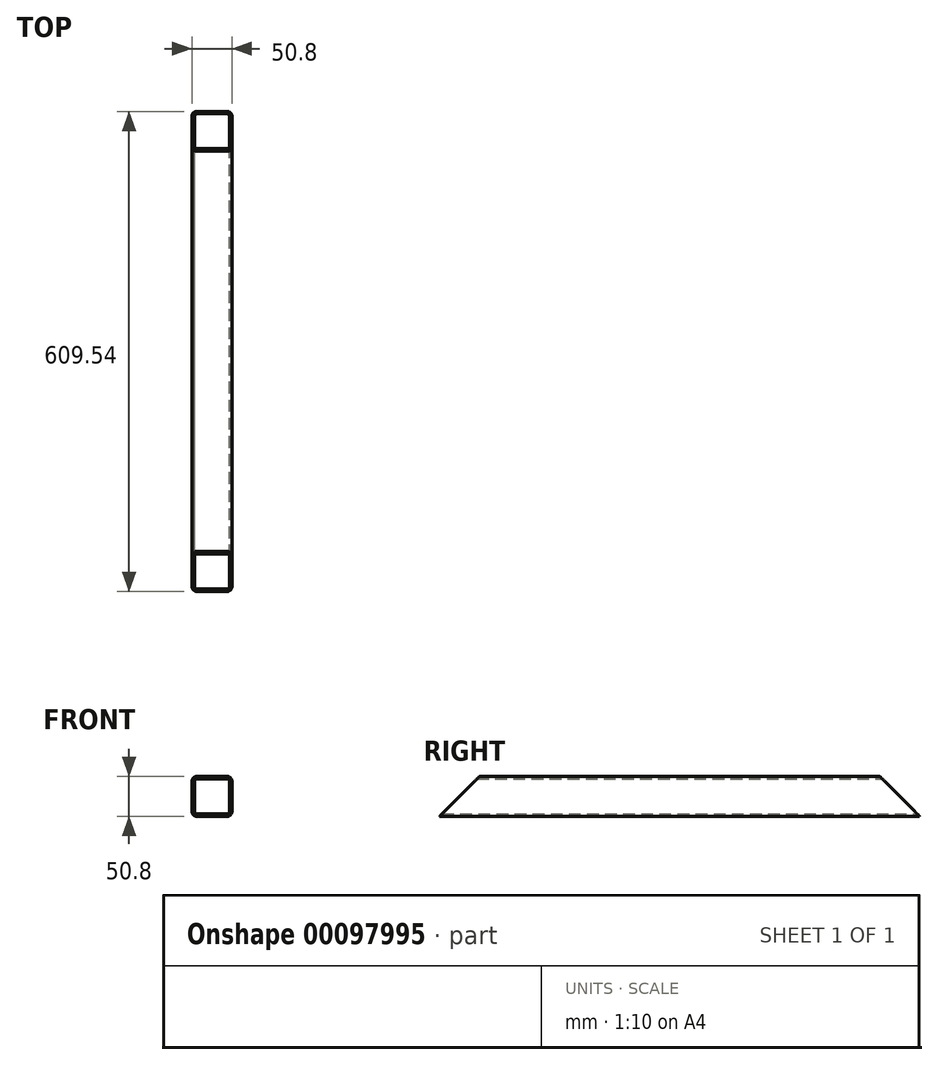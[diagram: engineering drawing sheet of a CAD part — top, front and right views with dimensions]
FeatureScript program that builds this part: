
annotation { "Feature Type Name" : "Feature", "Feature Type Description" : "" }
export const myFeature = defineFeature(function(context is Context, id is Id, definition is map)
    precondition{}
    {
        {
            var Q0;
            Q0=qCreatedBy(makeId("Front.planeOp"),FACE);
            var sketch = newSketch(context, id + "F0", { "sketchPlane" : qUnion([Q0])});
            skLineSegment(sketch, "E0.bottom", {"start": v(19.14, -25.27) * mm, "end": v(-18.96, -25.27) * mm});
            skLineSegment(sketch, "E0.top", {"start": v(19.14, 25.53) * mm, "end": v(-18.96, 25.53) * mm});
            skLineSegment(sketch, "E0.left", {"start": v(25.49, -18.92) * mm, "end": v(25.49, 19.18) * mm});
            skLineSegment(sketch, "E0.right", {"start": v(-25.31, -18.92) * mm, "end": v(-25.31, 19.18) * mm});
            skPoint(sketch, "E0.middle", {"position": v(0.09, 0.13) * mm});
            skLineSegment(sketch, "E1.bottom", {"start": v(19.14, 22.35) * mm, "end": v(-18.96, 22.35) * mm});
            skLineSegment(sketch, "E1.top", {"start": v(19.14, -22.1) * mm, "end": v(-18.96, -22.1) * mm});
            skLineSegment(sketch, "E1.left", {"start": v(22.31, 19.18) * mm, "end": v(22.31, -18.92) * mm});
            skLineSegment(sketch, "E1.right", {"start": v(-22.14, 19.18) * mm, "end": v(-22.14, -18.92) * mm});
            skPoint(sketch, "E2.visualSharp", {"position": v(-25.31, 25.53) * mm});
            skArc(sketch, "E2.filletArc", {"start": v(-18.96, 25.53) * mm, "mid": v(-23.45, 23.67) * mm, "end": v(-25.31, 19.18) * mm});
            skPoint(sketch, "E3.visualSharp", {"position": v(25.49, 25.53) * mm});
            skArc(sketch, "E3.filletArc", {"start": v(25.49, 19.18) * mm, "mid": v(23.63, 23.67) * mm, "end": v(19.14, 25.53) * mm});
            skPoint(sketch, "E4.visualSharp", {"position": v(25.49, -25.27) * mm});
            skArc(sketch, "E4.filletArc", {"start": v(19.14, -25.27) * mm, "mid": v(23.63, -23.41) * mm, "end": v(25.49, -18.92) * mm});
            skPoint(sketch, "E5.visualSharp", {"position": v(-25.31, -25.27) * mm});
            skArc(sketch, "E5.filletArc", {"start": v(-25.31, -18.92) * mm, "mid": v(-23.45, -23.41) * mm, "end": v(-18.96, -25.27) * mm});
            skPoint(sketch, "E6.visualSharp", {"position": v(22.31, 22.35) * mm});
            skArc(sketch, "E6.filletArc", {"start": v(22.31, 19.18) * mm, "mid": v(21.38, 21.42) * mm, "end": v(19.14, 22.35) * mm});
            skPoint(sketch, "E7.visualSharp", {"position": v(22.31, -22.1) * mm});
            skArc(sketch, "E7.filletArc", {"start": v(19.14, -22.1) * mm, "mid": v(21.38, -21.17) * mm, "end": v(22.31, -18.92) * mm});
            skPoint(sketch, "E8.visualSharp", {"position": v(-22.14, -22.1) * mm});
            skArc(sketch, "E8.filletArc", {"start": v(-22.14, -18.92) * mm, "mid": v(-21.2, -21.17) * mm, "end": v(-18.96, -22.1) * mm});
            skPoint(sketch, "E9.visualSharp", {"position": v(-22.14, 22.35) * mm});
            skArc(sketch, "E9.filletArc", {"start": v(-18.96, 22.35) * mm, "mid": v(-21.2, 21.42) * mm, "end": v(-22.14, 19.18) * mm});
            skSolve(sketch);
        }
        {
            var Q0;
            Q0=makeQuery(id+"F0.imprint","IMPRINT",FACE,{"disambiguationData":[TD([[makeQuery(id+"F0.imprint","IMPRINT",EDGE,{"derivedFrom":sQuery(id+"F0.wireOp",EDGE,"E0.bottom")}),-1.0]])]});
            extrude(context, id + "F1", {"entities" : qUnion([Q0]), "depth" : 609.6 * mm});
        }
        {
            var Q0;
            Q0=makeQuery(id+"F1.opExtrude","SWEPT_FACE",FACE,{"disambiguationData":[OSD([sQuery(id+"F0.wireOp",EDGE,"E0.left")])]});
            var sketch = newSketch(context, id + "F2", { "sketchPlane" : qUnion([Q0])});
            skLineSegment(sketch, "E10", {"start": v(-637.53, -53.26) * mm, "end": v(-529.68, 54.59) * mm});
            skLineSegment(sketch, "E11", {"start": v(-637.53, -53.26) * mm, "end": v(-637.53, 54.59) * mm});
            skLineSegment(sketch, "E12", {"start": v(-637.53, 54.59) * mm, "end": v(-529.68, 54.59) * mm});
            skLineSegment(sketch, "E13", {"start": v(48.87, -73.79) * mm, "end": v(-94.91, 69.99) * mm});
            skLineSegment(sketch, "E14", {"start": v(-94.91, 69.99) * mm, "end": v(48.87, 69.99) * mm});
            skLineSegment(sketch, "E15", {"start": v(48.87, 69.99) * mm, "end": v(48.87, -73.79) * mm});
            skSolve(sketch);
        }
        {
            var Q0;
            {var subQ6=sQuery(id+"F2.wireOp",EDGE,"E11");Q0=makeQuery(id+"F2.imprint","IMPRINT",FACE,{"disambiguationData":[TD([[makeQuery(id+"F2.imprint","IMPRINT",EDGE,{"derivedFrom":subQ6}),-1.0]])]});}
            var Q1;
            {var subQ1=sQuery(id+"F0.wireOp",EDGE,"E0.left");var subQ6=makeQuery(id+"F1.opExtrude","CAP_EDGE",EDGE,{"disambiguationData":[OSD([subQ1])],"isStart":false});Q1=makeQuery(id+"F2.imprint","IMPRINT",FACE,{"disambiguationData":[TD([[makeQuery(id+"F2.imprint","IMPRINT",EDGE,{"derivedFrom":subQ6}),-1.0]])]});}
            var Q2;
            {var subQ1=sQuery(id+"F2.wireOp",EDGE,"E14");Q2=makeQuery(id+"F2.imprint","IMPRINT",FACE,{"disambiguationData":[TD([[makeQuery(id+"F2.imprint","IMPRINT",EDGE,{"derivedFrom":subQ1}),-1.0]])]});}
            var Q3;
            {var subQ1=sQuery(id+"F0.wireOp",EDGE,"E0.left");var subQ6=makeQuery(id+"F1.opExtrude","CAP_EDGE",EDGE,{"disambiguationData":[OSD([subQ1])],"isStart":true});Q3=makeQuery(id+"F2.imprint","IMPRINT",FACE,{"disambiguationData":[TD([[makeQuery(id+"F2.imprint","IMPRINT",EDGE,{"derivedFrom":subQ6}),1.0]])]});}
            extrude(context, id + "F3", {"entities" : qUnion([Q0, Q1, Q2, Q3]), "operationType" : NewBodyOperationType.REMOVE, "endBound" : BoundingType.THROUGH_ALL, "oppositeDirection" : true, "depth" : 25.4 * mm});
        }
    });
